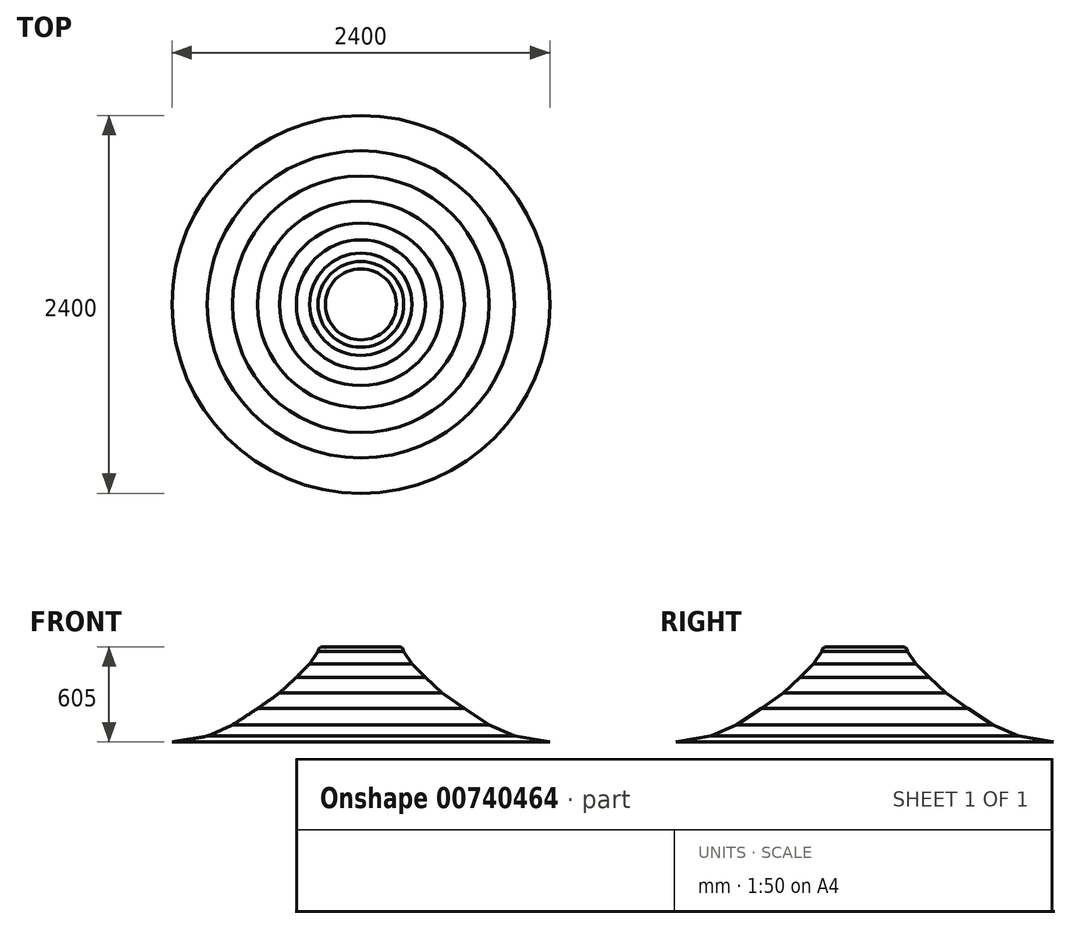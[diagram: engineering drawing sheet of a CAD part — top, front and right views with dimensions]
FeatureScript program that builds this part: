
annotation { "Feature Type Name" : "Feature", "Feature Type Description" : "" }
export const myFeature = defineFeature(function(context is Context, id is Id, definition is map)
    precondition{}
    {
        {
            var Q0;
            Q0=qCreatedBy(makeId("Front.planeOp"),FACE);
            var sketch = newSketch(context, id + "F0", { "sketchPlane" : qUnion([Q0])});
            skLineSegment(sketch, "E0", {"start": v(0, 0) * mm, "end": v(0, 600) * mm});
            skLineSegment(sketch, "E1", {"start": v(0, 600) * mm, "end": v(-255.52, 600) * mm});
            skLineSegment(sketch, "E2", {"start": v(-255.52, 600) * mm, "end": v(-324.88, 497.43) * mm});
            skLineSegment(sketch, "E3", {"start": v(-324.88, 497.43) * mm, "end": v(-409.98, 411.29) * mm});
            skLineSegment(sketch, "E4", {"start": v(-409.98, 411.29) * mm, "end": v(-516.28, 311.85) * mm});
            skLineSegment(sketch, "E5", {"start": v(-516.28, 311.85) * mm, "end": v(-656.86, 212.41) * mm});
            skLineSegment(sketch, "E6", {"start": v(-656.86, 212.41) * mm, "end": v(-814.59, 109.55) * mm});
            skLineSegment(sketch, "E7", {"start": v(-814.59, 109.55) * mm, "end": v(-975.75, 37.54) * mm});
            skLineSegment(sketch, "E8", {"start": v(-975.75, 37.54) * mm, "end": v(-1200, 0) * mm});
            skLineSegment(sketch, "E9", {"start": v(-1200, 0) * mm, "end": v(0, 0) * mm});
            skCircle(sketch, "E10", {"center": v(-242.24, 575) * mm, "radius": 30 * mm});
            skSolve(sketch);
        }
        {
            var Q0;
            Q0 = qSketchRegion(id + "F0", true);
            var Q1;
            Q1=sQuery(id+"F0.wireOp",EDGE,"E0");
            revolve(context, id + "F1", {"surfaceOperationType" : NewSurfaceOperationType.NEW, "entities" : qUnion([Q0]), "axis" : qUnion([Q1]), "revolveType" : RevolveType.FULL});
        }
    });
